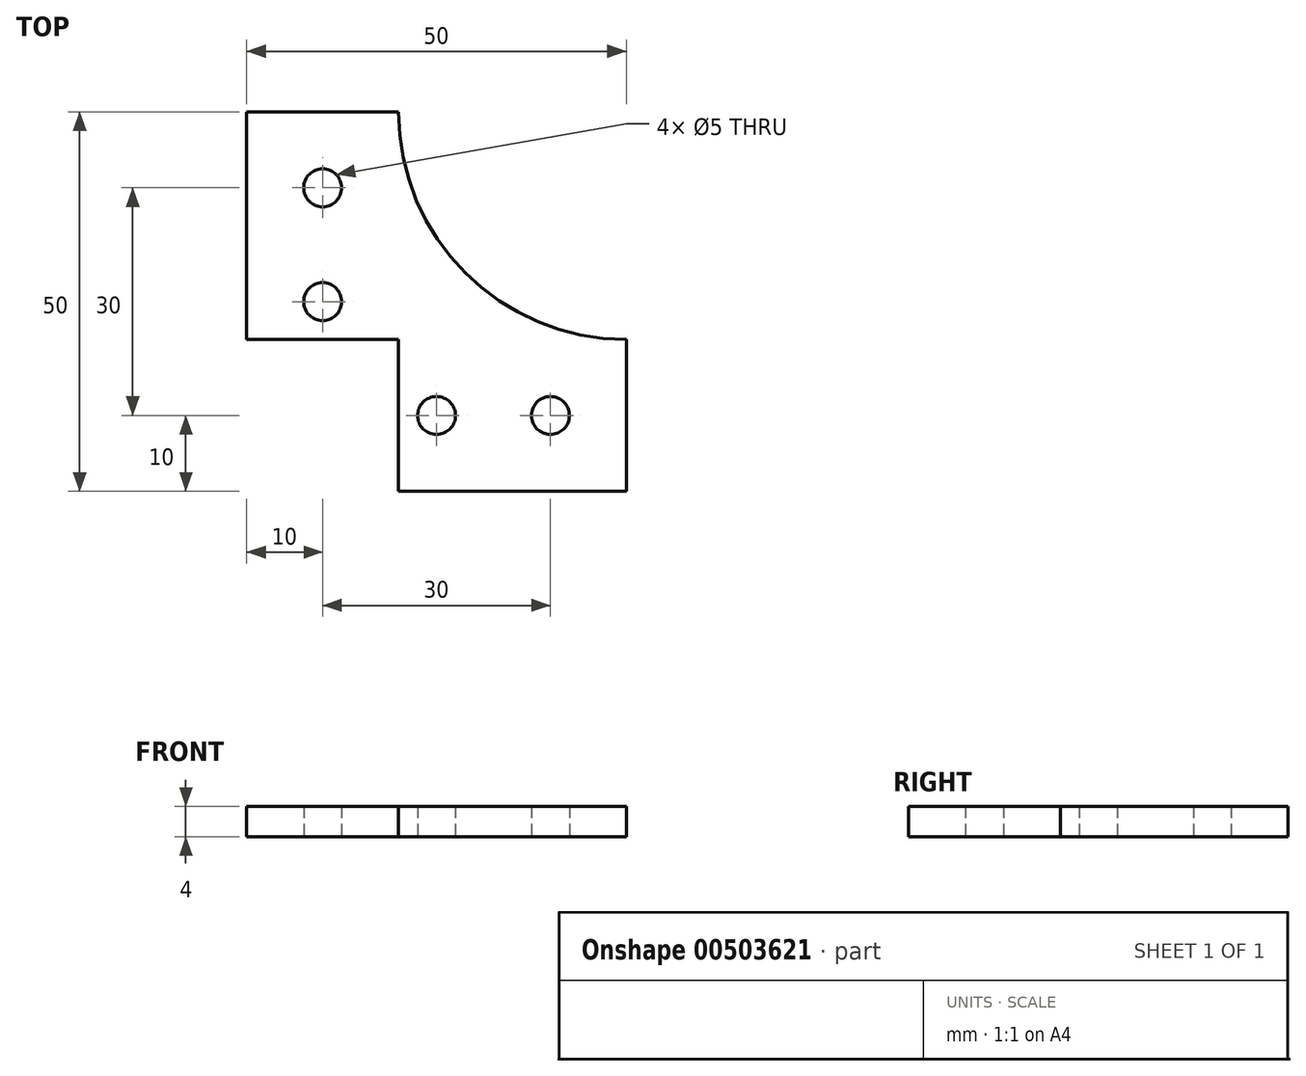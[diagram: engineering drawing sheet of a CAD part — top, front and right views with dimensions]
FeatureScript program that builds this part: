
annotation { "Feature Type Name" : "Feature", "Feature Type Description" : "" }
export const myFeature = defineFeature(function(context is Context, id is Id, definition is map)
    precondition{}
    {
        {
            var Q0;
            Q0=qCreatedBy(makeId("Top.planeOp"),FACE);
            var sketch = newSketch(context, id + "F0", { "sketchPlane" : qUnion([Q0])});
            skLineSegment(sketch, "E0.bottom", {"start": v(0, 0) * mm, "end": v(20, 0) * mm});
            skLineSegment(sketch, "E0.top", {"start": v(0, 50) * mm, "end": v(20, 50) * mm});
            skLineSegment(sketch, "E0.left", {"start": v(0, 0) * mm, "end": v(0, 50) * mm});
            skLineSegment(sketch, "E0.right", {"start": v(20, 0) * mm, "end": v(20, 50) * mm});
            skLineSegment(sketch, "E1.bottom", {"start": v(0, 0) * mm, "end": v(50, 0) * mm});
            skLineSegment(sketch, "E1.top", {"start": v(0, 20) * mm, "end": v(50, 20) * mm});
            skLineSegment(sketch, "E1.left", {"start": v(0, 0) * mm, "end": v(0, 20) * mm});
            skLineSegment(sketch, "E1.right", {"start": v(50, 0) * mm, "end": v(50, 20) * mm});
            skArc(sketch, "E2", {"start": v(20, 50) * mm, "mid": v(28.79, 28.79) * mm, "end": v(50, 20) * mm});
            skCircle(sketch, "E3", {"center": v(10, 10) * mm, "radius": 2.5 * mm});
            skPoint(sketch, "E3.centerSnap0", {"position": v(10, 0) * mm});
            skPoint(sketch, "E3.centerSnap1", {"position": v(0, 10) * mm});
            skCircle(sketch, "E4", {"center": v(10, 40) * mm, "radius": 2.5 * mm});
            skPoint(sketch, "E4.centerSnap0", {"position": v(10, 50) * mm});
            skCircle(sketch, "E5", {"center": v(40, 10) * mm, "radius": 2.5 * mm});
            skPoint(sketch, "E5.centerSnap0", {"position": v(50, 10) * mm});
            skLineSegment(sketch, "E6", {"start": v(10, 10) * mm, "end": v(40, 10) * mm, "construction": true});
            skLineSegment(sketch, "E7", {"start": v(10, 10) * mm, "end": v(10, 40) * mm, "construction": true});
            skCircle(sketch, "E8", {"center": v(10, 25) * mm, "radius": 2.5 * mm});
            skCircle(sketch, "E9", {"center": v(25, 10) * mm, "radius": 2.5 * mm});
            skSolve(sketch);
        }
        {
            var Q0;
            {var subQ1=sQuery(id+"F0.wireOp",EDGE,"E0.top");Q0=makeQuery(id+"F0.imprint","IMPRINT",FACE,{"disambiguationData":[TD([[makeQuery(id+"F0.imprint","IMPRINT",EDGE,{"derivedFrom":subQ1}),-1.0]])]});}
            var Q1;
            {var subQ0=sQuery(id+"F0.wireOp",EDGE,"E2");Q1=makeQuery(id+"F0.imprint","IMPRINT",FACE,{"disambiguationData":[TD([[makeQuery(id+"F0.imprint","IMPRINT",EDGE,{"derivedFrom":subQ0}),-1.0]])]});}
            var Q2;
            {var subQ0=sQuery(id+"F0.wireOp",EDGE,"E1.right");Q2=makeQuery(id+"F0.imprint","IMPRINT",FACE,{"disambiguationData":[TD([[makeQuery(id+"F0.imprint","IMPRINT",EDGE,{"derivedFrom":subQ0}),1.0]])]});}
            var Q3;
            {var subQ0=sQuery(id+"F0.wireOp",EDGE,"E1.left");Q3=makeQuery(id+"F0.imprint","IMPRINT",FACE,{"disambiguationData":[TD([[makeQuery(id+"F0.imprint","IMPRINT",EDGE,{"derivedFrom":subQ0}),-1.0]])]});}
            extrude(context, id + "F1", {"entities" : qUnion([Q0, Q1, Q2, Q3]), "depth" : 4 * mm, "offsetDistance" : 25 * mm});
        }
    });
